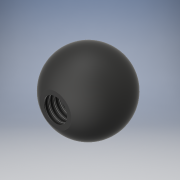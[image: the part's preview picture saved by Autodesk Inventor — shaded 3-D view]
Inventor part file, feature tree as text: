
AUTODESK INVENTOR PART (.ipt)
format: ipt  version: 2019 (Build 230136000, 136)  size: 138,752 bytes
history: native  units: mm
features: sketch x3, other x2, extrude x1, hole x1
ambient origin geometry x8: Origin, YZ Plane, XZ Plane, XY Plane, X Axis, Y Axis, Z Axis, Center Point
bodies: Solide1 (feature_tree)
feature tree (7):
  other  "Révolution1"
  other  "Plan de construction1"
  extrude  "Extrusion1"  Depth=5.0mm
  hole  "Perçage1"  [1 undecoded]
  sketch  "Esquisse1"
  sketch  "Esquisse2"
  sketch  "Esquisse3"
note: 1 required parameter value undecoded (feature->parameter linkage not recoverable at this tier; creation-order binding heuristic only, values carry confidence <= 0.55)
